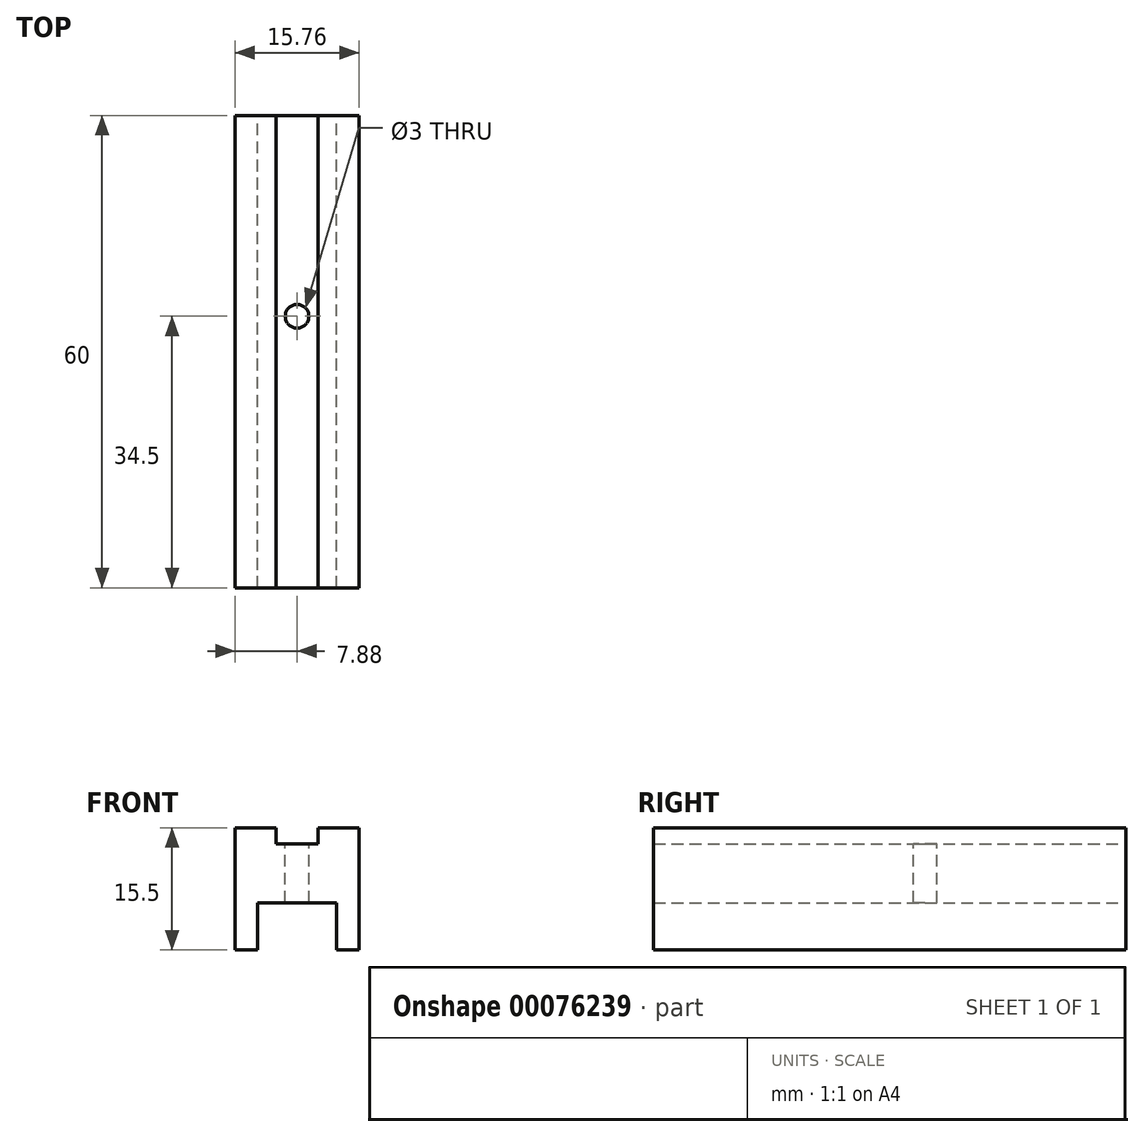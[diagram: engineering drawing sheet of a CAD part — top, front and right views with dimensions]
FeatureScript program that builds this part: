
annotation { "Feature Type Name" : "Feature", "Feature Type Description" : "" }
export const myFeature = defineFeature(function(context is Context, id is Id, definition is map)
    precondition{}
    {
        {
            var Q0;
            Q0=qCreatedBy(makeId("Front.planeOp"),FACE);
            var sketch = newSketch(context, id + "F0", { "sketchPlane" : qUnion([Q0])});
            skLineSegment(sketch, "E0", {"start": v(-7.88, -18.18) * mm, "end": v(-7.88, -2.68) * mm});
            skLineSegment(sketch, "E1", {"start": v(-7.88, -2.68) * mm, "end": v(-2.65, -2.68) * mm});
            skLineSegment(sketch, "E2", {"start": v(-2.65, -2.68) * mm, "end": v(-2.65, -4.68) * mm});
            skLineSegment(sketch, "E3", {"start": v(-2.65, -4.68) * mm, "end": v(2.65, -4.68) * mm});
            skLineSegment(sketch, "E4", {"start": v(2.65, -4.68) * mm, "end": v(2.65, -2.68) * mm});
            skLineSegment(sketch, "E5", {"start": v(2.65, -2.68) * mm, "end": v(7.88, -2.68) * mm});
            skLineSegment(sketch, "E6", {"start": v(7.88, -2.68) * mm, "end": v(7.88, -18.18) * mm});
            skLineSegment(sketch, "E7", {"start": v(7.87, -18.18) * mm, "end": v(5, -18.18) * mm});
            skLineSegment(sketch, "E8", {"start": v(5, -18.18) * mm, "end": v(5, -12.18) * mm});
            skLineSegment(sketch, "E9", {"start": v(5, -12.18) * mm, "end": v(-5, -12.18) * mm});
            skLineSegment(sketch, "E10", {"start": v(-5, -12.18) * mm, "end": v(-5, -18.18) * mm});
            skLineSegment(sketch, "E11", {"start": v(-5, -18.18) * mm, "end": v(-7.87, -18.18) * mm});
            skSolve(sketch);
        }
        {
            var Q0;
            Q0 = qSketchRegion(id + "F0", true);
            extrude(context, id + "F1", {"entities" : qUnion([Q0]), "endBound" : BoundingType.SYMMETRIC, "depth" : 60 * mm});
        }
        {
            var Q0;
            Q0=makeQuery(id+"F1.opExtrude","SWEPT_FACE",FACE,{"disambiguationData":[OSD([sQuery(id+"F0.wireOp",EDGE,"E3")])]});
            var sketch = newSketch(context, id + "F2", { "sketchPlane" : qUnion([Q0])});
            skCircle(sketch, "E12", {"center": v(0, 4.5) * mm, "radius": 1.5 * mm});
            skSolve(sketch);
        }
        {
            var Q0;
            Q0 = qSketchRegion(id + "F2", true);
            extrude(context, id + "F3", {"entities" : qUnion([Q0]), "operationType" : NewBodyOperationType.REMOVE, "oppositeDirection" : true, "depth" : 25 * mm});
        }
    });
